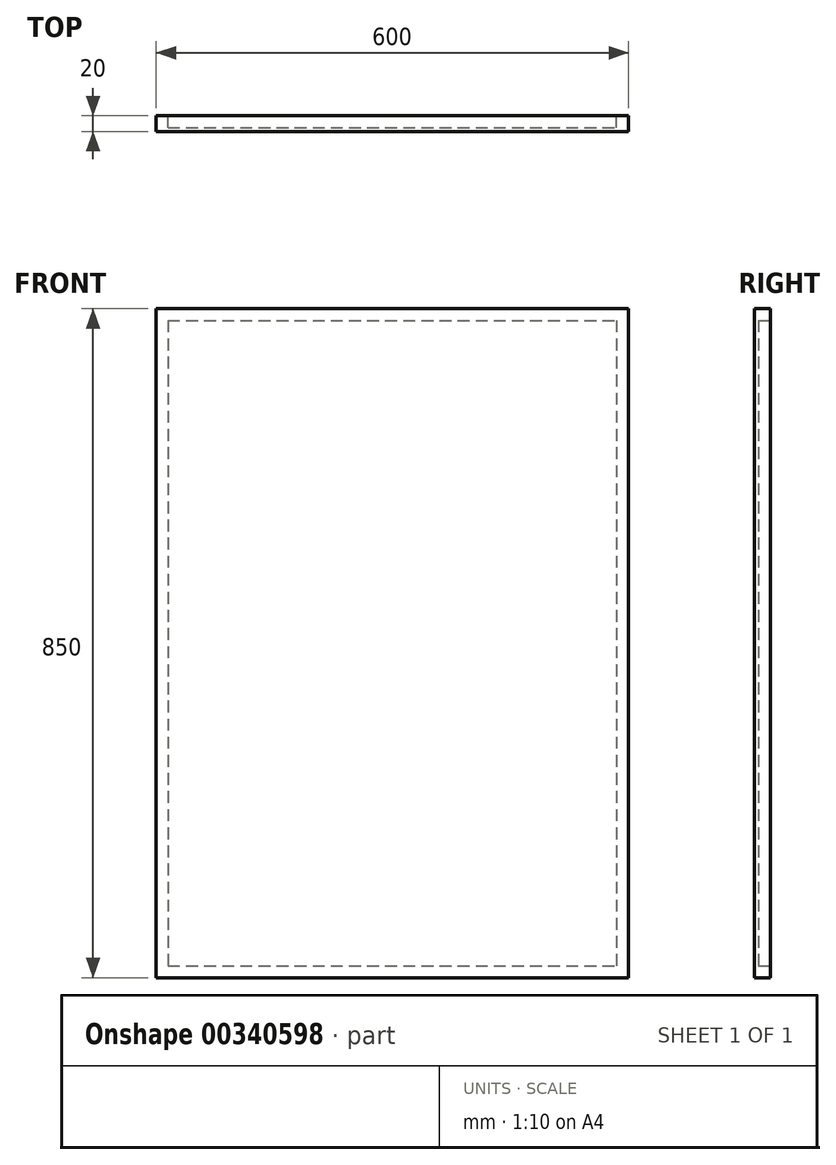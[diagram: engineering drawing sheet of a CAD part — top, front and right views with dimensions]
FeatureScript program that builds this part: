
annotation { "Feature Type Name" : "Feature", "Feature Type Description" : "" }
export const myFeature = defineFeature(function(context is Context, id is Id, definition is map)
    precondition{}
    {
        {
            var Q0;
            Q0=qCreatedBy(makeId("Front.planeOp"),FACE);
            var sketch = newSketch(context, id + "F0", { "sketchPlane" : qUnion([Q0])});
            skLineSegment(sketch, "E0.bottom", {"start": v(-39.41, 785.08) * mm, "end": v(560.59, 785.08) * mm});
            skLineSegment(sketch, "E0.top", {"start": v(-39.41, -64.92) * mm, "end": v(560.59, -64.92) * mm});
            skLineSegment(sketch, "E0.left", {"start": v(-39.41, 785.08) * mm, "end": v(-39.41, -64.92) * mm});
            skLineSegment(sketch, "E0.right", {"start": v(560.59, 785.08) * mm, "end": v(560.59, -64.92) * mm});
            skLineSegment(sketch, "E1.0", {"start": v(-24.41, 770.08) * mm, "end": v(545.59, 770.08) * mm});
            skLineSegment(sketch, "E1.1", {"start": v(-24.41, 770.08) * mm, "end": v(-24.41, -49.92) * mm});
            skLineSegment(sketch, "E1.2", {"start": v(-24.41, -49.92) * mm, "end": v(545.59, -49.92) * mm});
            skLineSegment(sketch, "E1.3", {"start": v(545.59, 770.08) * mm, "end": v(545.59, -49.92) * mm});
            skSolve(sketch);
        }
        {
            var Q0;
            Q0 = qSketchRegion(id + "F0", true);
            extrude(context, id + "F1", {"entities" : qUnion([Q0]), "depth" : 20 * mm});
        }
        {
            var Q0;
            Q0=makeQuery(id+"F1.opExtrude","CAP_FACE",FACE,{"disambiguationData":[OSD([sQuery(id+"F0.wireOp",EDGE,"E0.bottom"),sQuery(id+"F0.wireOp",EDGE,"E0.top"),sQuery(id+"F0.wireOp",EDGE,"E0.left"),sQuery(id+"F0.wireOp",EDGE,"E0.right"),sQuery(id+"F0.wireOp",EDGE,"E1.0"),sQuery(id+"F0.wireOp",EDGE,"E1.1"),sQuery(id+"F0.wireOp",EDGE,"E1.2"),sQuery(id+"F0.wireOp",EDGE,"E1.3")])],"isStart":false});
            var sketch = newSketch(context, id + "F2", { "sketchPlane" : qUnion([Q0])});
            skLineSegment(sketch, "E2.bottom", {"start": v(-39.41, 785.08) * mm, "end": v(560.59, 785.08) * mm});
            skLineSegment(sketch, "E2.top", {"start": v(-39.41, -64.92) * mm, "end": v(560.59, -64.92) * mm});
            skLineSegment(sketch, "E2.left", {"start": v(-39.41, 785.08) * mm, "end": v(-39.41, -64.92) * mm});
            skLineSegment(sketch, "E2.right", {"start": v(560.59, 785.08) * mm, "end": v(560.59, -64.92) * mm});
            skSolve(sketch);
        }
        {
            var Q0;
            Q0 = qSketchRegion(id + "F2", true);
            extrude(context, id + "F3", {"entities" : qUnion([Q0]), "operationType" : NewBodyOperationType.ADD, "oppositeDirection" : true, "depth" : 5 * mm});
        }
    });
